# Revit family: Haworth_BeHold_Wardrobe
name_source: partatom
category: Furniture Systems
revit_build: Autodesk Revit 2018 (Build: 20170223_1515(x64)
units: mm (PartAtom-declared; Revit-internal decimal feet)

## family parameters
Always vertical = Yes
Cut with Voids When Loaded = No
OmniClass Number = 23.40.70.14.64.21
OmniClass Title = Systems Furniture
Part Type = Normal
Room Calculation Point = No
Round Connector Dimension = Use Diameter
Shared = No
Work Plane-Based = No

## types (4) — shared parameters
Actual Depth = 30"
Actual Height = 65"
Assembly Code = E2020200
Bottom Case Offset = 1/2"
Bottom Drawer Offset = 1 3/8"
Case Edge Finish = Haworth _ Laminate _ Beige H-34
Case Finish = Haworth _ Laminate _ Beige H-34
Case Thickness = 3/4"
Classic Pull = No
Classic Pull Length = 6 3/4"
Cresent Pull = No
Custom Size = No
Depth = 30"
Description = Haworth - Be_Hold - Wardrobe
Door Height = 62 91/128"
Fixed Shelf 1 Offset = 15 11/16"
Front Edge Finish = Haworth _ Laminate _ Beige H-34
Front Finish = Haworth _ Laminate _ Beige H-34
Glide Finish = Haworth _ Polymer _ Slate
Height = 65"
Left Panel Edge Finish = Haworth _ Laminate _ Beige H-34
Left Panel Finish = Haworth _ Laminate _ Beige H-34
Linear Pull = No
Linear Pull Length = 8"
Lock Side Offset = 2 1/4"
Lock Top Offset = 32 155/256"
Manufacturer = Haworth
Max. Depth = 30"
Max. Height = 65"
Min. Depth = 16"
Min. Height = 41"
Model = Haworth Be_Hold
No Pull = No
Pull Finish = Haworth _ Paint _ Smooth Plaster
Pull Height Centerline = 32 155/256"
Pull Side Offset = 0"
Revision Number = 1
Right Panel Edge Finish = Haworth _ Laminate _ Beige H-34
Right Panel Finish = Haworth _ Laminate _ Beige H-34
Separate Shelf Offset = 9 1/16"
Size = Verify Final Dim. w/ Haworth
Standard Depths = 16, 18, 24, 30 in.
Standard Double Doors Widths = 24 in.
Standard Heights = 41, 49, 57, 65 in.
Standard Single Door Widths = 12, 15, 18 in.
Sustainability Info = https://www.haworth.com
Top Thickness = 3/4"
Trim Finish = Haworth _ Paint _ Smooth Plaster
URL = www.haworth.com
Warranty = http://www.haworth.com
Wing Door Pull Length = 16 3/4"
Wing Pull = Yes
With Lock = Yes

## per-type parameters (varying)
| type | Actual Width | Back Case Back Control | Back Case Side Control | Door Width | Double Doors | Five High | Fixed Shelf Control | Four High | Inset Style | Max. Width | Mid Separator Control | Min. Width | Proud Style | Side Case Back Control | Single Door | Six High | Three High | Top Case Back Control | URL - Product | Width |
| Double Doors - 24w 30d 65h - Inset Back | 24" | 3/16" | 3/4" | 11 7/8" | Yes | No | No | No | Yes | 24" | Yes | 24" | No | 0" | No | Yes | No | 3/16" | https://www.haworth.com | 24" |
| Single Door - 18w 30d 65h - Proud Back | 18" | 0" | 0" | 17 7/8" | No | Yes | Yes | Yes | No | 18" | No | 12" | Yes | 3/4" | Yes | No | Yes | 0" |  | 18" |
| Single Door - 15w 30d 65h - Proud Back | 15" | 0" | 0" | 14 7/8" | No | Yes | No | Yes | No | 18" | No | 12" | Yes | 3/4" | Yes | No | Yes | 0" |  | 15" |
| Single Door - 12w 30d 65h - Inset Back | 12" | 3/16" | 3/4" | 11 7/8" | No | Yes | No | Yes | Yes | 18" | No | 12" | No | 0" | Yes | No | Yes | 3/16" |  | 12" |

## geometry (parser evidence)
native form markers: Sweep x8
no freeform markers — native parametric forms only
